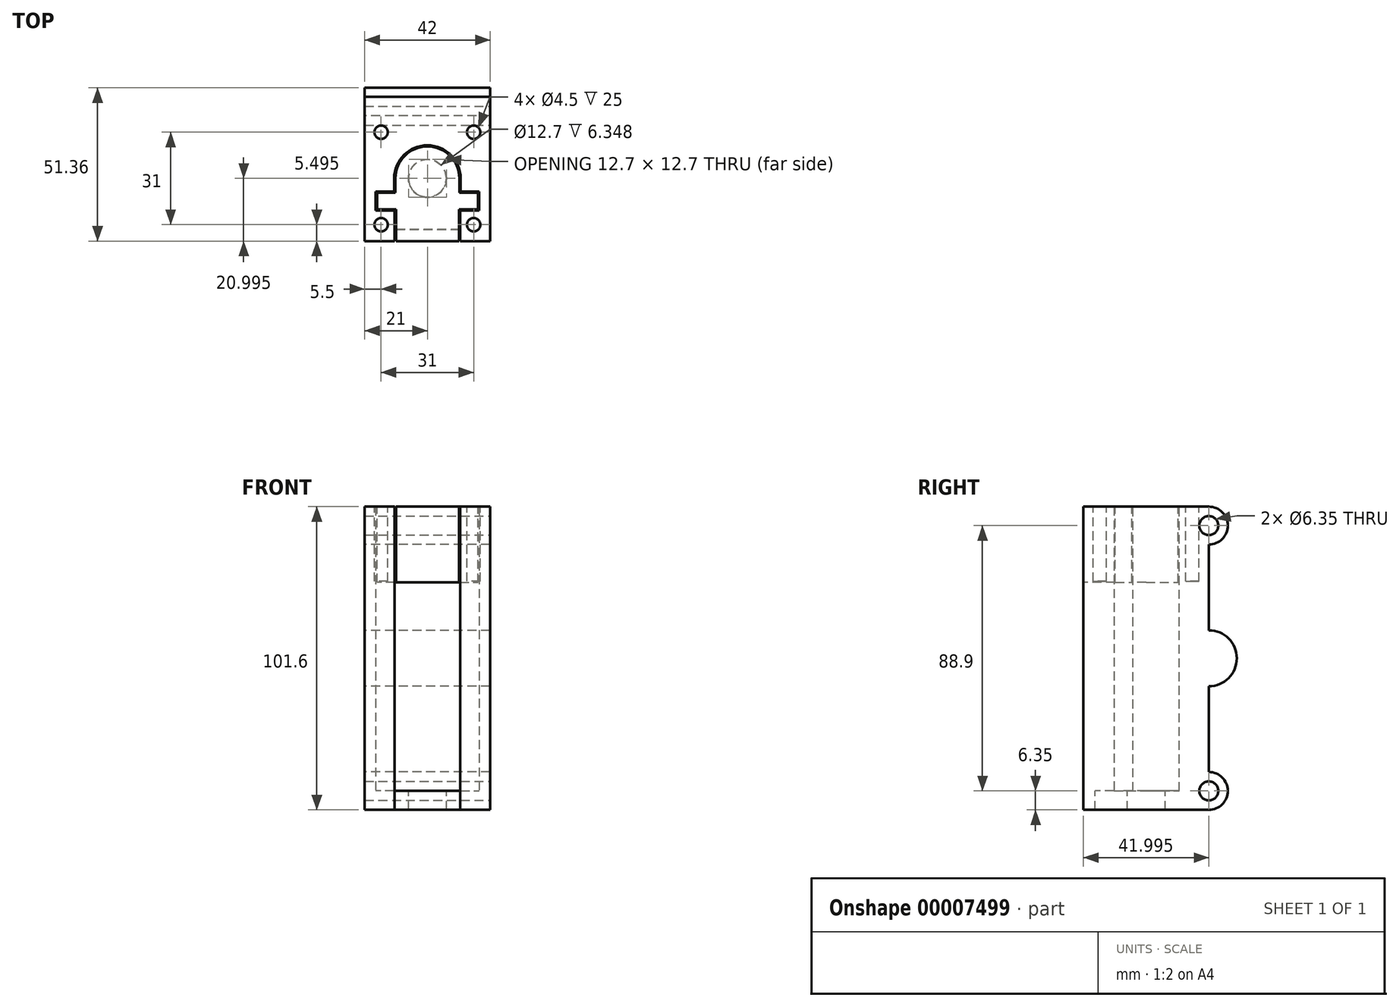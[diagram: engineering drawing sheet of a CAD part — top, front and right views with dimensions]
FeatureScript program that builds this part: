
annotation { "Feature Type Name" : "Feature", "Feature Type Description" : "" }
export const myFeature = defineFeature(function(context is Context, id is Id, definition is map)
    precondition{}
    {
        {
            var Q0;
            Q0=qCreatedBy(makeId("Right.planeOp"),FACE);
            var sketch = newSketch(context, id + "F0", { "sketchPlane" : qUnion([Q0])});
            skLineSegment(sketch, "E0.rect.bottom", {"start": v(9.52, 50.8) * mm, "end": v(-9.53, 50.8) * mm});
            skLineSegment(sketch, "E0.rect.top", {"start": v(9.52, -50.8) * mm, "end": v(-9.52, -50.8) * mm});
            skLineSegment(sketch, "E0.rect.left", {"start": v(9.52, 50.8) * mm, "end": v(9.53, -50.8) * mm});
            skLineSegment(sketch, "E0.rect.right", {"start": v(-9.53, 50.8) * mm, "end": v(-9.52, -50.8) * mm});
            skPoint(sketch, "E0.rect.middle", {"position": v(0, 0) * mm});
            skCircle(sketch, "E1", {"center": v(9.53, 0) * mm, "radius": 9.37 * mm});
            skCircle(sketch, "E2", {"center": v(9.53, 44.45) * mm, "radius": 6.35 * mm});
            skCircle(sketch, "E3", {"center": v(9.53, -44.45) * mm, "radius": 6.35 * mm});
            skLineSegment(sketch, "E4", {"start": v(-32, 0) * mm, "end": v(39.5, 0) * mm, "construction": true});
            skSolve(sketch);
        }
        {
            var Q0;
            {var subQ3=sQuery(id+"F0.wireOp",EDGE,"E0.rect.bottom");Q0=makeQuery(id+"F0.imprint","IMPRINT",FACE,{"disambiguationData":[TD([[makeQuery(id+"F0.imprint","IMPRINT",EDGE,{"derivedFrom":subQ3}),1.0]])]});}
            var Q1;
            {var subQ0=sQuery(id+"F0.wireOp",EDGE,"E2");var subQ1=sQuery(id+"F0.wireOp",EDGE,"E0.rect.left");var subQ2=makeQuery(id+"F0.imprint","INTERSECT",VERTEX,{"derivedFrom":[subQ1,subQ0]});Q1=makeQuery(id+"F0.imprint","IMPRINT",FACE,{"disambiguationData":[TD([[makeQuery(id+"F0.imprint","IMPRINT",EDGE,{"disambiguationData":[TD([[subQ2,1.0]])],"derivedFrom":subQ1}),-1.0]])]});}
            var Q2;
            {var subQ0=sQuery(id+"F0.wireOp",EDGE,"E2");var subQ1=sQuery(id+"F0.wireOp",EDGE,"E0.rect.left");var subQ2=makeQuery(id+"F0.imprint","INTERSECT",VERTEX,{"derivedFrom":[subQ1,subQ0]});Q2=makeQuery(id+"F0.imprint","IMPRINT",FACE,{"disambiguationData":[TD([[makeQuery(id+"F0.imprint","IMPRINT",EDGE,{"disambiguationData":[TD([[subQ2,1.0]])],"derivedFrom":subQ1}),1.0]])]});}
            var Q3;
            {var subQ0=sQuery(id+"F0.wireOp",EDGE,"E1");var subQ1=sQuery(id+"F0.wireOp",EDGE,"E0.rect.left");var subQ3=makeQuery(id+"F0.imprint","INTERSECT",VERTEX,{"disambiguationData":[OD(0.0)],"derivedFrom":[subQ1,subQ0]});Q3=makeQuery(id+"F0.imprint","IMPRINT",FACE,{"disambiguationData":[TD([[makeQuery(id+"F0.imprint","IMPRINT",EDGE,{"disambiguationData":[TD([[subQ3,-1.0]])],"derivedFrom":subQ1}),-1.0]])]});}
            var Q4;
            {var subQ0=sQuery(id+"F0.wireOp",EDGE,"E1");var subQ1=sQuery(id+"F0.wireOp",EDGE,"E0.rect.left");var subQ3=makeQuery(id+"F0.imprint","INTERSECT",VERTEX,{"disambiguationData":[OD(0.0)],"derivedFrom":[subQ1,subQ0]});Q4=makeQuery(id+"F0.imprint","IMPRINT",FACE,{"disambiguationData":[TD([[makeQuery(id+"F0.imprint","IMPRINT",EDGE,{"disambiguationData":[TD([[subQ3,-1.0]])],"derivedFrom":subQ1}),1.0]])]});}
            var Q5;
            {var subQ0=sQuery(id+"F0.wireOp",EDGE,"E3");var subQ1=sQuery(id+"F0.wireOp",EDGE,"E0.rect.left");var subQ2=makeQuery(id+"F0.imprint","INTERSECT",VERTEX,{"derivedFrom":[subQ1,subQ0]});Q5=makeQuery(id+"F0.imprint","IMPRINT",FACE,{"disambiguationData":[TD([[makeQuery(id+"F0.imprint","IMPRINT",EDGE,{"disambiguationData":[TD([[subQ2,-1.0]])],"derivedFrom":subQ1}),-1.0]])]});}
            var Q6;
            {var subQ0=sQuery(id+"F0.wireOp",EDGE,"E3");var subQ1=sQuery(id+"F0.wireOp",EDGE,"E0.rect.left");var subQ2=makeQuery(id+"F0.imprint","INTERSECT",VERTEX,{"derivedFrom":[subQ1,subQ0]});Q6=makeQuery(id+"F0.imprint","IMPRINT",FACE,{"disambiguationData":[TD([[makeQuery(id+"F0.imprint","IMPRINT",EDGE,{"disambiguationData":[TD([[subQ2,-1.0]])],"derivedFrom":subQ1}),1.0]])]});}
            var Q7;
            Q7=qNothing();
            var Q8;
            Q8=qNothing();
            extrude(context, id + "F1", {"entities" : qUnion([Q0, Q1, Q2, Q3, Q4, Q5, Q6]), "surfaceEntities" : qUnion([Q7, Q8]), "endBound" : BoundingType.SYMMETRIC, "depth" : 42 * mm});
        }
        {
            var Q0;
            Q0=makeQuery(id+"F1.opExtrude","CAP_FACE",FACE,{"disambiguationData":[OSD([sQuery(id+"F0.wireOp",EDGE,"E0.rect.bottom"),sQuery(id+"F0.wireOp",EDGE,"E0.rect.top"),sQuery(id+"F0.wireOp",EDGE,"E0.rect.left"),sQuery(id+"F0.wireOp",EDGE,"E0.rect.right"),sQuery(id+"F0.wireOp",EDGE,"E1"),sQuery(id+"F0.wireOp",EDGE,"E2"),sQuery(id+"F0.wireOp",EDGE,"E3")])],"isStart":false});
            var sketch = newSketch(context, id + "F2", { "sketchPlane" : qUnion([Q0])});
            skCircle(sketch, "E5", {"center": v(9.53, 44.45) * mm, "radius": 3.18 * mm});
            skCircle(sketch, "E6", {"center": v(9.53, -44.45) * mm, "radius": 3.18 * mm});
            skSolve(sketch);
        }
        {
            var Q0;
            Q0 = qSketchRegion(id + "F2", true);
            extrude(context, id + "F3", {"entities" : qUnion([Q0]), "operationType" : NewBodyOperationType.REMOVE, "endBound" : BoundingType.THROUGH_ALL, "oppositeDirection" : true, "depth" : 25 * mm});
        }
        {
            var Q0;
            Q0=makeQuery(id+"F1.opExtrude","SWEPT_FACE",FACE,{"disambiguationData":[OSD([sQuery(id+"F0.wireOp",EDGE,"E0.rect.bottom")])]});
            var sketch = newSketch(context, id + "F4", { "sketchPlane" : qUnion([Q0])});
            skLineSegment(sketch, "E7.bottom", {"start": v(-21, 9.52) * mm, "end": v(21, 9.52) * mm});
            skLineSegment(sketch, "E7.top", {"start": v(-21, -32.48) * mm, "end": v(21, -32.48) * mm});
            skLineSegment(sketch, "E7.left", {"start": v(-21, 9.52) * mm, "end": v(-21, -32.48) * mm});
            skLineSegment(sketch, "E7.right", {"start": v(21, 9.52) * mm, "end": v(21, -32.48) * mm});
            skSolve(sketch);
        }
        {
            var Q0;
            {var subQ2=sQuery(id+"F4.wireOp",EDGE,"E7.top");Q0=makeQuery(id+"F4.imprint","IMPRINT",FACE,{"disambiguationData":[TD([[makeQuery(id+"F4.imprint","IMPRINT",EDGE,{"derivedFrom":subQ2}),1.0]])]});}
            extrude(context, id + "F5", {"entities" : qUnion([Q0]), "operationType" : NewBodyOperationType.ADD, "oppositeDirection" : true, "depth" : 6.35 * mm});
        }
        {
            var Q0;
            Q0=makeQuery(id+"F1.opExtrude","SWEPT_FACE",FACE,{"disambiguationData":[OSD([sQuery(id+"F0.wireOp",EDGE,"E0.rect.top")])]});
            var sketch = newSketch(context, id + "F6", { "sketchPlane" : qUnion([Q0])});
            skLineSegment(sketch, "E8.bottom", {"start": v(21, -9.53) * mm, "end": v(-21, -9.53) * mm});
            skLineSegment(sketch, "E8.top", {"start": v(21, 32.48) * mm, "end": v(-21, 32.48) * mm});
            skLineSegment(sketch, "E8.left", {"start": v(21, -9.53) * mm, "end": v(21, 32.48) * mm});
            skLineSegment(sketch, "E8.right", {"start": v(-21, -9.53) * mm, "end": v(-21, 32.48) * mm});
            skSolve(sketch);
        }
        {
            var Q0;
            {var subQ2=sQuery(id+"F6.wireOp",EDGE,"E8.top");Q0=makeQuery(id+"F6.imprint","IMPRINT",FACE,{"disambiguationData":[TD([[makeQuery(id+"F6.imprint","IMPRINT",EDGE,{"derivedFrom":subQ2}),1.0]])]});}
            extrude(context, id + "F7", {"entities" : qUnion([Q0]), "operationType" : NewBodyOperationType.ADD, "oppositeDirection" : true, "depth" : 6.35 * mm});
        }
        {
            var Q0;
            {var subQ0=sQuery(id+"F0.wireOp",EDGE,"E0.rect.bottom");Q0=makeQuery(id+"F5.boolean.opBoolean","MERGE",FACE,{"derivedFrom":[makeQuery(id+"F1.opExtrude","SWEPT_FACE",FACE,{"disambiguationData":[OSD([subQ0])]}),makeQuery(id+"F5.opExtrude","CAP_FACE",FACE,{"disambiguationData":[OSD([subQ0,sQuery(id+"F0.wireOp",EDGE,"E0.rect.right"),sQuery(id+"F4.wireOp",EDGE,"E7.top"),sQuery(id+"F4.wireOp",EDGE,"E7.left"),sQuery(id+"F4.wireOp",EDGE,"E7.right")])],"isStart":true})]});}
            var sketch = newSketch(context, id + "F8", { "sketchPlane" : qUnion([Q0])});
            skLineSegment(sketch, "E9", {"start": v(-21, 9.53) * mm, "end": v(21, -32.48) * mm, "construction": true});
            skLineSegment(sketch, "E10", {"start": v(-21, -32.48) * mm, "end": v(21, 9.53) * mm, "construction": true});
            skCircle(sketch, "E11", {"center": v(0, -11.48) * mm, "radius": 11.11 * mm});
            skSolve(sketch);
        }
        {
            var Q0;
            Q0 = qSketchRegion(id + "F8", true);
            var Q1;
            Q1=makeQuery(id+"F7.opExtrude","CAP_FACE",FACE,{"disambiguationData":[OSD([sQuery(id+"F0.wireOp",EDGE,"E0.rect.top"),sQuery(id+"F0.wireOp",EDGE,"E0.rect.right"),sQuery(id+"F6.wireOp",EDGE,"E8.top"),sQuery(id+"F6.wireOp",EDGE,"E8.left"),sQuery(id+"F6.wireOp",EDGE,"E8.right")])],"isStart":false});
            extrude(context, id + "F9", {"entities" : qUnion([Q0]), "operationType" : NewBodyOperationType.REMOVE, "endBound" : BoundingType.UP_TO_SURFACE, "oppositeDirection" : true, "endBoundEntityFace" : qUnion([Q1]), "depth" : 25 * mm});
        }
        {
            var Q0;
            Q0=makeQuery(id+"F9.boolean.opBoolean","MERGE",FACE,{"derivedFrom":[makeQuery(id+"F7.opExtrude","CAP_FACE",FACE,{"disambiguationData":[OSD([sQuery(id+"F0.wireOp",EDGE,"E0.rect.top"),sQuery(id+"F0.wireOp",EDGE,"E0.rect.right"),sQuery(id+"F6.wireOp",EDGE,"E8.top"),sQuery(id+"F6.wireOp",EDGE,"E8.left"),sQuery(id+"F6.wireOp",EDGE,"E8.right")])],"isStart":false}),makeQuery(id+"F9.opExtrude","CAP_FACE",FACE,{"disambiguationData":[OSD([sQuery(id+"F8.wireOp",EDGE,"E11")])],"isStart":false})]});
            var sketch = newSketch(context, id + "F10", { "sketchPlane" : qUnion([Q0])});
            skCircle(sketch, "E12", {"center": v(0, -11.48) * mm, "radius": 7.94 * mm});
            skSolve(sketch);
        }
        {
            var Q0;
            Q0 = qSketchRegion(id + "F10", true);
            extrude(context, id + "F11", {"entities" : qUnion([Q0]), "operationType" : NewBodyOperationType.REMOVE, "oppositeDirection" : true, "depth" : 1 / 406.4 * mm});
        }
        {
            var Q0;
            Q0=makeQuery(id+"F11.boolean.opBoolean","COPY",FACE,{"derivedFrom":makeQuery(id+"F11.opExtrude","CAP_FACE",FACE,{"disambiguationData":[OSD([sQuery(id+"F10.wireOp",EDGE,"E12")])],"isStart":false})});
            var sketch = newSketch(context, id + "F12", { "sketchPlane" : qUnion([Q0])});
            skCircle(sketch, "E13", {"center": v(0, -11.48) * mm, "radius": 6.35 * mm});
            skSolve(sketch);
        }
        {
            var Q0;
            Q0=makeQuery(id+"F9.boolean.opBoolean","MERGE",FACE,{"derivedFrom":[makeQuery(id+"F7.opExtrude","CAP_FACE",FACE,{"disambiguationData":[OSD([sQuery(id+"F0.wireOp",EDGE,"E0.rect.top"),sQuery(id+"F0.wireOp",EDGE,"E0.rect.right"),sQuery(id+"F6.wireOp",EDGE,"E8.top"),sQuery(id+"F6.wireOp",EDGE,"E8.left"),sQuery(id+"F6.wireOp",EDGE,"E8.right")])],"isStart":false}),makeQuery(id+"F9.opExtrude","CAP_FACE",FACE,{"disambiguationData":[OSD([sQuery(id+"F8.wireOp",EDGE,"E11")])],"isStart":false})]});
            var sketch = newSketch(context, id + "F13", { "sketchPlane" : qUnion([Q0])});
            skLineSegment(sketch, "E14.bottom", {"start": v(-21, -9.52) * mm, "end": v(-10.94, -9.52) * mm});
            skLineSegment(sketch, "E14.top", {"start": v(-21, -28.57) * mm, "end": v(-10.94, -28.57) * mm});
            skLineSegment(sketch, "E14.left", {"start": v(-21, -9.52) * mm, "end": v(-21, -28.57) * mm});
            skLineSegment(sketch, "E14.right", {"start": v(-10.94, -9.52) * mm, "end": v(-10.94, -28.57) * mm});
            skLineSegment(sketch, "E15.bottom", {"start": v(21, -9.52) * mm, "end": v(10.94, -9.52) * mm});
            skLineSegment(sketch, "E15.top", {"start": v(21, -28.57) * mm, "end": v(10.94, -28.57) * mm});
            skLineSegment(sketch, "E15.left", {"start": v(21, -9.52) * mm, "end": v(21, -28.57) * mm});
            skLineSegment(sketch, "E15.right", {"start": v(10.94, -9.52) * mm, "end": v(10.94, -28.57) * mm});
            skLineSegment(sketch, "E16", {"start": v(-31.37, -19.05) * mm, "end": v(27.45, -19.05) * mm, "construction": true});
            skLineSegment(sketch, "E17.bottom", {"start": v(-10.94, -22.23) * mm, "end": v(-17.3, -22.23) * mm});
            skLineSegment(sketch, "E17.top", {"start": v(-10.94, -15.88) * mm, "end": v(-17.3, -15.88) * mm});
            skLineSegment(sketch, "E17.left", {"start": v(-10.94, -22.23) * mm, "end": v(-10.94, -15.88) * mm, "construction": true});
            skLineSegment(sketch, "E17.right", {"start": v(-17.3, -22.23) * mm, "end": v(-17.3, -15.88) * mm});
            skLineSegment(sketch, "E18.bottom", {"start": v(10.94, -22.22) * mm, "end": v(17.3, -22.22) * mm});
            skLineSegment(sketch, "E18.top", {"start": v(10.94, -15.87) * mm, "end": v(17.3, -15.87) * mm});
            skLineSegment(sketch, "E18.left", {"start": v(10.94, -22.22) * mm, "end": v(10.94, -15.87) * mm});
            skLineSegment(sketch, "E18.right", {"start": v(17.3, -22.22) * mm, "end": v(17.3, -15.87) * mm});
            skSolve(sketch);
        }
        {
            var Q0;
            {var subQ4=sQuery(id+"F13.wireOp",EDGE,"E14.bottom");Q0=makeQuery(id+"F13.imprint","IMPRINT",FACE,{"disambiguationData":[TD([[makeQuery(id+"F13.imprint","IMPRINT",EDGE,{"derivedFrom":subQ4}),1.0]])]});}
            var Q1;
            {var subQ5=sQuery(id+"F13.wireOp",EDGE,"E15.bottom");Q1=makeQuery(id+"F13.imprint","IMPRINT",FACE,{"disambiguationData":[TD([[makeQuery(id+"F13.imprint","IMPRINT",EDGE,{"derivedFrom":subQ5}),1.0]])]});}
            var Q2;
            Q2=makeQuery(id+"F5.opExtrude","CAP_FACE",FACE,{"disambiguationData":[OSD([sQuery(id+"F0.wireOp",EDGE,"E0.rect.bottom"),sQuery(id+"F0.wireOp",EDGE,"E0.rect.right"),sQuery(id+"F4.wireOp",EDGE,"E7.top"),sQuery(id+"F4.wireOp",EDGE,"E7.left"),sQuery(id+"F4.wireOp",EDGE,"E7.right")])],"isStart":false});
            extrude(context, id + "F14", {"entities" : qUnion([Q0, Q1]), "operationType" : NewBodyOperationType.ADD, "endBound" : BoundingType.UP_TO_SURFACE, "endBoundEntityFace" : qUnion([Q2]), "depth" : 25 * mm});
        }
        {
            var Q0;
            Q0=makeQuery(id+"F9.boolean.opBoolean","MERGE",FACE,{"derivedFrom":[makeQuery(id+"F7.opExtrude","CAP_FACE",FACE,{"disambiguationData":[OSD([sQuery(id+"F0.wireOp",EDGE,"E0.rect.top"),sQuery(id+"F0.wireOp",EDGE,"E0.rect.right"),sQuery(id+"F6.wireOp",EDGE,"E8.top"),sQuery(id+"F6.wireOp",EDGE,"E8.left"),sQuery(id+"F6.wireOp",EDGE,"E8.right")])],"isStart":false}),makeQuery(id+"F9.opExtrude","CAP_FACE",FACE,{"disambiguationData":[OSD([sQuery(id+"F8.wireOp",EDGE,"E11")])],"isStart":false})]});
            var sketch = newSketch(context, id + "F15", { "sketchPlane" : qUnion([Q0])});
            skLineSegment(sketch, "E19.bottom", {"start": v(-21, -28.57) * mm, "end": v(21, -28.57) * mm});
            skLineSegment(sketch, "E19.top", {"start": v(-21, -32.48) * mm, "end": v(21, -32.48) * mm});
            skLineSegment(sketch, "E19.left", {"start": v(-21, -28.57) * mm, "end": v(-21, -32.48) * mm});
            skLineSegment(sketch, "E19.right", {"start": v(21, -28.57) * mm, "end": v(21, -32.48) * mm});
            skSolve(sketch);
        }
        {
            var Q0;
            Q0 = qSketchRegion(id + "F15", true);
            extrude(context, id + "F16", {"entities" : qUnion([Q0]), "operationType" : NewBodyOperationType.REMOVE, "endBound" : BoundingType.THROUGH_ALL, "oppositeDirection" : true, "depth" : 25 * mm});
        }
        {
            var Q0;
            Q0 = qSketchRegion(id + "F12", true);
            extrude(context, id + "F17", {"entities" : qUnion([Q0]), "operationType" : NewBodyOperationType.REMOVE, "endBound" : BoundingType.THROUGH_ALL, "oppositeDirection" : true, "depth" : 3 / 406.4 * mm});
        }
        {
            var Q0;
            Q0=makeQuery(id+"F5.opExtrude","CAP_FACE",FACE,{"disambiguationData":[OSD([sQuery(id+"F0.wireOp",EDGE,"E0.rect.bottom"),sQuery(id+"F0.wireOp",EDGE,"E0.rect.right"),sQuery(id+"F4.wireOp",EDGE,"E7.top"),sQuery(id+"F4.wireOp",EDGE,"E7.left"),sQuery(id+"F4.wireOp",EDGE,"E7.right")])],"isStart":false});
            var sketch = newSketch(context, id + "F18", { "sketchPlane" : qUnion([Q0])});
            skLineSegment(sketch, "E20.bottom", {"start": v(-10.94, 28.57) * mm, "end": v(10.94, 28.57) * mm});
            skLineSegment(sketch, "E20.top", {"start": v(-10.94, 32.48) * mm, "end": v(10.94, 32.48) * mm});
            skLineSegment(sketch, "E20.left", {"start": v(-10.94, 28.57) * mm, "end": v(-10.94, 32.48) * mm});
            skLineSegment(sketch, "E20.right", {"start": v(10.94, 28.57) * mm, "end": v(10.94, 32.48) * mm});
            skSolve(sketch);
        }
        {
            var Q0;
            Q0 = qSketchRegion(id + "F18", true);
            var Q1;
            Q1=makeQuery(id+"F18.imprint","IMPRINT",FACE,{"disambiguationData":[TD([[makeQuery(id+"F18.imprint","IMPRINT",EDGE,{"derivedFrom":sQuery(id+"F18.wireOp",EDGE,"E20.bottom")}),-1.0]])]});
            extrude(context, id + "F19", {"entities" : qUnion([Q0, Q1]), "operationType" : NewBodyOperationType.REMOVE, "oppositeDirection" : true, "depth" : 25 * mm});
        }
        {
            var Q0;
            {var subQ0=sQuery(id+"F0.wireOp",EDGE,"E0.rect.bottom");Q0=makeQuery(id+"F5.boolean.opBoolean","MERGE",FACE,{"derivedFrom":[makeQuery(id+"F1.opExtrude","SWEPT_FACE",FACE,{"disambiguationData":[OSD([subQ0])]}),makeQuery(id+"F5.opExtrude","CAP_FACE",FACE,{"disambiguationData":[OSD([subQ0,sQuery(id+"F0.wireOp",EDGE,"E0.rect.right"),sQuery(id+"F4.wireOp",EDGE,"E7.top"),sQuery(id+"F4.wireOp",EDGE,"E7.left"),sQuery(id+"F4.wireOp",EDGE,"E7.right")])],"isStart":true})]});}
            var sketch = newSketch(context, id + "F20", { "sketchPlane" : qUnion([Q0])});
            skCircle(sketch, "E21", {"center": v(0, -11.48) * mm, "radius": 11.11 * mm});
            skSolve(sketch);
        }
        {
            var Q0;
            {var subQ0=sQuery(id+"F20.wireOp",EDGE,"E21");var subQ1=sQuery(id+"F0.wireOp",EDGE,"E0.rect.bottom");var subQ2=makeQuery(id+"F5.boolean.opBoolean","MERGE",FACE,{"derivedFrom":[makeQuery(id+"F1.opExtrude","SWEPT_FACE",FACE,{"disambiguationData":[OSD([subQ1])]}),makeQuery(id+"F5.opExtrude","CAP_FACE",FACE,{"disambiguationData":[OSD([subQ1,sQuery(id+"F0.wireOp",EDGE,"E0.rect.right"),sQuery(id+"F4.wireOp",EDGE,"E7.top"),sQuery(id+"F4.wireOp",EDGE,"E7.left"),sQuery(id+"F4.wireOp",EDGE,"E7.right")])],"isStart":true})]});var subQ4=makeQuery(id+"F20.imprint","INTERSECT",VERTEX,{"derivedFrom":[makeQuery(id+"F19.boolean.opBoolean","INTERSECT",EDGE,{"derivedFrom":[subQ2,makeQuery(id+"F19.opExtrude","SWEPT_FACE",FACE,{"disambiguationData":[OSD([sQuery(id+"F13.wireOp",EDGE,"E14.right")])]})]}),subQ0]});Q0=makeQuery(id+"F20.imprint","IMPRINT",FACE,{"disambiguationData":[TD([[makeQuery(id+"F20.imprint","IMPRINT",EDGE,{"disambiguationData":[TD([[subQ4,-1.0]])],"derivedFrom":subQ0}),1.0]])]});}
            var Q1;
            Q1=makeQuery(id+"F9.boolean.opBoolean","MERGE",FACE,{"derivedFrom":[makeQuery(id+"F7.opExtrude","CAP_FACE",FACE,{"disambiguationData":[OSD([sQuery(id+"F0.wireOp",EDGE,"E0.rect.top"),sQuery(id+"F0.wireOp",EDGE,"E0.rect.right"),sQuery(id+"F6.wireOp",EDGE,"E8.top"),sQuery(id+"F6.wireOp",EDGE,"E8.left"),sQuery(id+"F6.wireOp",EDGE,"E8.right")])],"isStart":false}),makeQuery(id+"F9.opExtrude","CAP_FACE",FACE,{"disambiguationData":[OSD([sQuery(id+"F8.wireOp",EDGE,"E11")])],"isStart":false})]});
            extrude(context, id + "F21", {"entities" : qUnion([Q0]), "operationType" : NewBodyOperationType.REMOVE, "endBound" : BoundingType.UP_TO_SURFACE, "oppositeDirection" : true, "endBoundEntityFace" : qUnion([Q1]), "depth" : 25 * mm});
        }
        {
            var Q0;
            {var subQ0=sQuery(id+"F0.wireOp",EDGE,"E0.rect.bottom");Q0=makeQuery(id+"F5.boolean.opBoolean","MERGE",FACE,{"derivedFrom":[makeQuery(id+"F1.opExtrude","SWEPT_FACE",FACE,{"disambiguationData":[OSD([subQ0])]}),makeQuery(id+"F5.opExtrude","CAP_FACE",FACE,{"disambiguationData":[OSD([subQ0,sQuery(id+"F0.wireOp",EDGE,"E0.rect.right"),sQuery(id+"F4.wireOp",EDGE,"E7.top"),sQuery(id+"F4.wireOp",EDGE,"E7.left"),sQuery(id+"F4.wireOp",EDGE,"E7.right")])],"isStart":true})]});}
            var sketch = newSketch(context, id + "F22", { "sketchPlane" : qUnion([Q0])});
            skLineSegment(sketch, "E22.bottom", {"start": v(-11.11, -11.48) * mm, "end": v(11.11, -11.48) * mm});
            skLineSegment(sketch, "E22.top", {"start": v(-11.11, -32.48) * mm, "end": v(11.11, -32.48) * mm});
            skLineSegment(sketch, "E22.left", {"start": v(-11.11, -11.48) * mm, "end": v(-11.11, -32.48) * mm});
            skLineSegment(sketch, "E22.right", {"start": v(11.11, -11.48) * mm, "end": v(11.11, -32.48) * mm});
            skCircle(sketch, "E23", {"center": v(0, -11.48) * mm, "radius": 3.92 * mm, "construction": true});
            skSolve(sketch);
        }
        {
            var Q0;
            {var subQ0=sQuery(id+"F0.wireOp",EDGE,"E0.rect.bottom");var subQ1=makeQuery(id+"F5.boolean.opBoolean","MERGE",FACE,{"derivedFrom":[makeQuery(id+"F1.opExtrude","SWEPT_FACE",FACE,{"disambiguationData":[OSD([subQ0])]}),makeQuery(id+"F5.opExtrude","CAP_FACE",FACE,{"disambiguationData":[OSD([subQ0,sQuery(id+"F0.wireOp",EDGE,"E0.rect.right"),sQuery(id+"F4.wireOp",EDGE,"E7.top"),sQuery(id+"F4.wireOp",EDGE,"E7.left"),sQuery(id+"F4.wireOp",EDGE,"E7.right")])],"isStart":true})]});var subQ5=makeQuery(id+"F19.boolean.opBoolean","INTERSECT",EDGE,{"derivedFrom":[subQ1,makeQuery(id+"F19.opExtrude","SWEPT_FACE",FACE,{"disambiguationData":[OSD([sQuery(id+"F13.wireOp",EDGE,"E14.right")])]})]});Q0=makeQuery(id+"F22.imprint","IMPRINT",FACE,{"disambiguationData":[TD([[makeQuery(id+"F22.imprint","IMPRINT",EDGE,{"derivedFrom":subQ5}),-1.0]])]});}
            var Q1;
            {var subQ0=sQuery(id+"F0.wireOp",EDGE,"E0.rect.bottom");var subQ1=makeQuery(id+"F5.boolean.opBoolean","MERGE",FACE,{"derivedFrom":[makeQuery(id+"F1.opExtrude","SWEPT_FACE",FACE,{"disambiguationData":[OSD([subQ0])]}),makeQuery(id+"F5.opExtrude","CAP_FACE",FACE,{"disambiguationData":[OSD([subQ0,sQuery(id+"F0.wireOp",EDGE,"E0.rect.right"),sQuery(id+"F4.wireOp",EDGE,"E7.top"),sQuery(id+"F4.wireOp",EDGE,"E7.left"),sQuery(id+"F4.wireOp",EDGE,"E7.right")])],"isStart":true})]});var subQ5=makeQuery(id+"F19.boolean.opBoolean","INTERSECT",EDGE,{"derivedFrom":[subQ1,makeQuery(id+"F19.opExtrude","SWEPT_FACE",FACE,{"disambiguationData":[OSD([sQuery(id+"F13.wireOp",EDGE,"E15.right")])]})]});Q1=makeQuery(id+"F22.imprint","IMPRINT",FACE,{"disambiguationData":[TD([[makeQuery(id+"F22.imprint","IMPRINT",EDGE,{"derivedFrom":subQ5}),1.0]])]});}
            var Q2;
            Q2=makeQuery(id+"F21.boolean.opBoolean","MERGE",FACE,{"derivedFrom":[makeQuery(id+"F9.boolean.opBoolean","MERGE",FACE,{"derivedFrom":[makeQuery(id+"F7.opExtrude","CAP_FACE",FACE,{"disambiguationData":[OSD([sQuery(id+"F0.wireOp",EDGE,"E0.rect.top"),sQuery(id+"F0.wireOp",EDGE,"E0.rect.right"),sQuery(id+"F6.wireOp",EDGE,"E8.top"),sQuery(id+"F6.wireOp",EDGE,"E8.left"),sQuery(id+"F6.wireOp",EDGE,"E8.right")])],"isStart":false}),makeQuery(id+"F9.opExtrude","CAP_FACE",FACE,{"disambiguationData":[OSD([sQuery(id+"F8.wireOp",EDGE,"E11")])],"isStart":false})]}),makeQuery(id+"F21.opExtrude","CAP_FACE",FACE,{"disambiguationData":[OSD([sQuery(id+"F20.wireOp",EDGE,"E21")])],"isStart":false})]});
            extrude(context, id + "F23", {"entities" : qUnion([Q0, Q1]), "operationType" : NewBodyOperationType.REMOVE, "endBound" : BoundingType.UP_TO_SURFACE, "oppositeDirection" : true, "endBoundEntityFace" : qUnion([Q2]), "depth" : 25 * mm});
        }
        {
            var Q0;
            {var subQ0=sQuery(id+"F0.wireOp",EDGE,"E0.rect.bottom");Q0=makeQuery(id+"F5.boolean.opBoolean","MERGE",FACE,{"derivedFrom":[makeQuery(id+"F1.opExtrude","SWEPT_FACE",FACE,{"disambiguationData":[OSD([subQ0])]}),makeQuery(id+"F5.opExtrude","CAP_FACE",FACE,{"disambiguationData":[OSD([subQ0,sQuery(id+"F0.wireOp",EDGE,"E0.rect.right"),sQuery(id+"F4.wireOp",EDGE,"E7.top"),sQuery(id+"F4.wireOp",EDGE,"E7.left"),sQuery(id+"F4.wireOp",EDGE,"E7.right")])],"isStart":true})]});}
            var sketch = newSketch(context, id + "F24", { "sketchPlane" : qUnion([Q0])});
            skLineSegment(sketch, "E24", {"start": v(-10.94, -32.48) * mm, "end": v(10.94, -32.48) * mm, "construction": true});
            skLineSegment(sketch, "E25.0", {"start": v(10.72, -11.48) * mm, "end": v(10.72, -16.27) * mm});
            skLineSegment(sketch, "E25.1", {"start": v(10.72, -16.27) * mm, "end": v(16.9, -16.27) * mm});
            skLineSegment(sketch, "E25.2", {"start": v(16.9, -21.83) * mm, "end": v(16.9, -16.27) * mm});
            skLineSegment(sketch, "E25.3", {"start": v(10.54, -21.83) * mm, "end": v(16.9, -21.83) * mm});
            skLineSegment(sketch, "E25.4", {"start": v(10.54, -21.83) * mm, "end": v(10.54, -32.08) * mm});
            skArc(sketch, "E25.5", {"start": v(10.72, -11.48) * mm, "mid": v(0, -0.76) * mm, "end": v(-10.72, -11.48) * mm});
            skLineSegment(sketch, "E25.6", {"start": v(-10.54, -32.08) * mm, "end": v(10.54, -32.08) * mm});
            skLineSegment(sketch, "E25.7", {"start": v(-10.54, -21.83) * mm, "end": v(-10.54, -32.08) * mm});
            skLineSegment(sketch, "E25.8", {"start": v(-10.54, -21.83) * mm, "end": v(-16.9, -21.83) * mm});
            skLineSegment(sketch, "E25.9", {"start": v(-16.9, -21.83) * mm, "end": v(-16.9, -16.27) * mm});
            skLineSegment(sketch, "E25.10", {"start": v(-10.72, -16.27) * mm, "end": v(-16.9, -16.27) * mm});
            skLineSegment(sketch, "E25.11", {"start": v(-10.72, -11.48) * mm, "end": v(-10.72, -16.27) * mm});
            skLineSegment(sketch, "E26.top", {"start": v(-10.54, -32.48) * mm, "end": v(10.54, -32.48) * mm});
            skLineSegment(sketch, "E26.left", {"start": v(-10.54, -32.08) * mm, "end": v(-10.54, -32.48) * mm});
            skLineSegment(sketch, "E26.right", {"start": v(10.54, -32.08) * mm, "end": v(10.54, -32.48) * mm});
            skSolve(sketch);
        }
        {
            var Q0;
            Q0=makeQuery(id+"F24.imprint","IMPRINT",FACE,{"disambiguationData":[TD([[makeQuery(id+"F24.imprint","IMPRINT",EDGE,{"derivedFrom":sQuery(id+"F24.wireOp",EDGE,"E25.0")}),-1.0]])]});
            var Q1;
            Q1=makeQuery(id+"F24.imprint","IMPRINT",FACE,{"disambiguationData":[TD([[makeQuery(id+"F24.imprint","IMPRINT",EDGE,{"derivedFrom":sQuery(id+"F24.wireOp",EDGE,"E25.6")}),-1.0]])]});
            extrude(context, id + "F25", {"entities" : qUnion([Q0, Q1]), "oppositeDirection" : true, "depth" : 25.4 * mm});
        }
        {
            var Q0;
            {var subQ0=sQuery(id+"F0.wireOp",EDGE,"E0.rect.bottom");Q0=makeQuery(id+"F5.boolean.opBoolean","MERGE",FACE,{"derivedFrom":[makeQuery(id+"F1.opExtrude","SWEPT_FACE",FACE,{"disambiguationData":[OSD([subQ0])]}),makeQuery(id+"F5.opExtrude","CAP_FACE",FACE,{"disambiguationData":[OSD([subQ0,sQuery(id+"F0.wireOp",EDGE,"E0.rect.right"),sQuery(id+"F4.wireOp",EDGE,"E7.top"),sQuery(id+"F4.wireOp",EDGE,"E7.left"),sQuery(id+"F4.wireOp",EDGE,"E7.right")])],"isStart":true})]});}
            var sketch = newSketch(context, id + "F26", { "sketchPlane" : qUnion([Q0])});
            skCircle(sketch, "E27", {"center": v(0, -11.48) * mm, "radius": 3.49 * mm, "construction": true});
            skLineSegment(sketch, "E28", {"start": v(0, -11.48) * mm, "end": v(35.4, -11.48) * mm, "construction": true});
            skLineSegment(sketch, "E29", {"start": v(0, -11.48) * mm, "end": v(27.21, 15.74) * mm, "construction": true});
            skCircle(sketch, "E30", {"center": v(15.5, 4.02) * mm, "radius": 2.25 * mm});
            skCircle(sketch, "E31.1.0", {"center": v(-15.5, 4.02) * mm, "radius": 2.25 * mm});
            skCircle(sketch, "E31.2.0", {"center": v(-15.5, -26.98) * mm, "radius": 2.25 * mm});
            skCircle(sketch, "E31.3.0", {"center": v(15.5, -26.97) * mm, "radius": 2.25 * mm});
            skSolve(sketch);
        }
        {
            var Q0;
            {var subQ0=sQuery(id+"F0.wireOp",EDGE,"E0.rect.bottom");var subQ1=sQuery(id+"F0.wireOp",EDGE,"E0.rect.right");var subQ2=sQuery(id+"F4.wireOp",EDGE,"E7.top");var subQ3=sQuery(id+"F4.wireOp",EDGE,"E7.left");Q0=makeQuery(id+"F19.boolean.opBoolean","SPLIT",FACE,{"disambiguationData":[TD([makeQuery(id+"F5.opExtrude","SWEPT_FACE",FACE,{"disambiguationData":[OSD([subQ3])]})])],"derivedFrom":makeQuery(id+"F5.opExtrude","CAP_FACE",FACE,{"disambiguationData":[OSD([subQ0,subQ1,subQ2,subQ3,sQuery(id+"F4.wireOp",EDGE,"E7.right")])],"isStart":false})});}
            var sketch = newSketch(context, id + "F27", { "sketchPlane" : qUnion([Q0])});
            skLineSegment(sketch, "E32.bottom", {"start": v(-21, 32.48) * mm, "end": v(-10.94, 32.48) * mm});
            skLineSegment(sketch, "E32.top", {"start": v(-21, 28.57) * mm, "end": v(-10.94, 28.57) * mm});
            skLineSegment(sketch, "E32.left", {"start": v(-21, 32.48) * mm, "end": v(-21, 28.57) * mm});
            skLineSegment(sketch, "E32.right", {"start": v(-10.94, 32.48) * mm, "end": v(-10.94, 28.57) * mm});
            skLineSegment(sketch, "E33.bottom", {"start": v(10.94, 32.48) * mm, "end": v(21, 32.48) * mm});
            skLineSegment(sketch, "E33.top", {"start": v(10.94, 28.57) * mm, "end": v(21, 28.57) * mm});
            skLineSegment(sketch, "E33.left", {"start": v(10.94, 32.48) * mm, "end": v(10.94, 28.57) * mm});
            skLineSegment(sketch, "E33.right", {"start": v(21, 32.48) * mm, "end": v(21, 28.57) * mm});
            skSolve(sketch);
        }
        {
            var Q0;
            Q0 = qSketchRegion(id + "F27", true);
            var Q1;
            {var subQ0=sQuery(id+"F0.wireOp",EDGE,"E0.rect.top");Q1=makeQuery(id+"F7.boolean.opBoolean","MERGE",FACE,{"derivedFrom":[makeQuery(id+"F1.opExtrude","SWEPT_FACE",FACE,{"disambiguationData":[OSD([subQ0])]}),makeQuery(id+"F7.opExtrude","CAP_FACE",FACE,{"disambiguationData":[OSD([subQ0,sQuery(id+"F0.wireOp",EDGE,"E0.rect.right"),sQuery(id+"F6.wireOp",EDGE,"E8.top"),sQuery(id+"F6.wireOp",EDGE,"E8.left"),sQuery(id+"F6.wireOp",EDGE,"E8.right")])],"isStart":true})]});}
            extrude(context, id + "F28", {"entities" : qUnion([Q0]), "operationType" : NewBodyOperationType.ADD, "endBound" : BoundingType.UP_TO_SURFACE, "endBoundEntityFace" : qUnion([Q1]), "depth" : 25 * mm});
        }
        {
            var Q0;
            Q0 = qSketchRegion(id + "F26", true);
            extrude(context, id + "F29", {"entities" : qUnion([Q0]), "operationType" : NewBodyOperationType.REMOVE, "oppositeDirection" : true, "depth" : 25 * mm});
        }
    });
